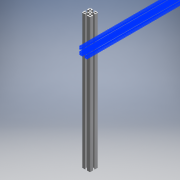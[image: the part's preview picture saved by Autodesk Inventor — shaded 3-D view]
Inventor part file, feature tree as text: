
AUTODESK INVENTOR PART (.ipt)
format: ipt  version: 2019 (Build 230136000, 136)  size: 310,272 bytes
history: native  units: mm
features: other x4, extrude x1, sketch x1, reference x1
ambient origin geometry x8: Origin, YZ Plane, XZ Plane, XY Plane, X Axis, Y Axis, Z Axis, Center Point
bodies: Body1 (feature_tree)
feature tree (7):
  other  "솔리드1"
  extrude  "돌출1"  Depth=500.0mm TaperAngle=0.0deg
  sketch  "스케치1"
  reference  "참조1"
  other  "<userpath>\Documents\Inventor\Projects\2019_CapstoneDesign\Body.iam"
  other  "Body.iam"
  other  "Propile_800:1"
